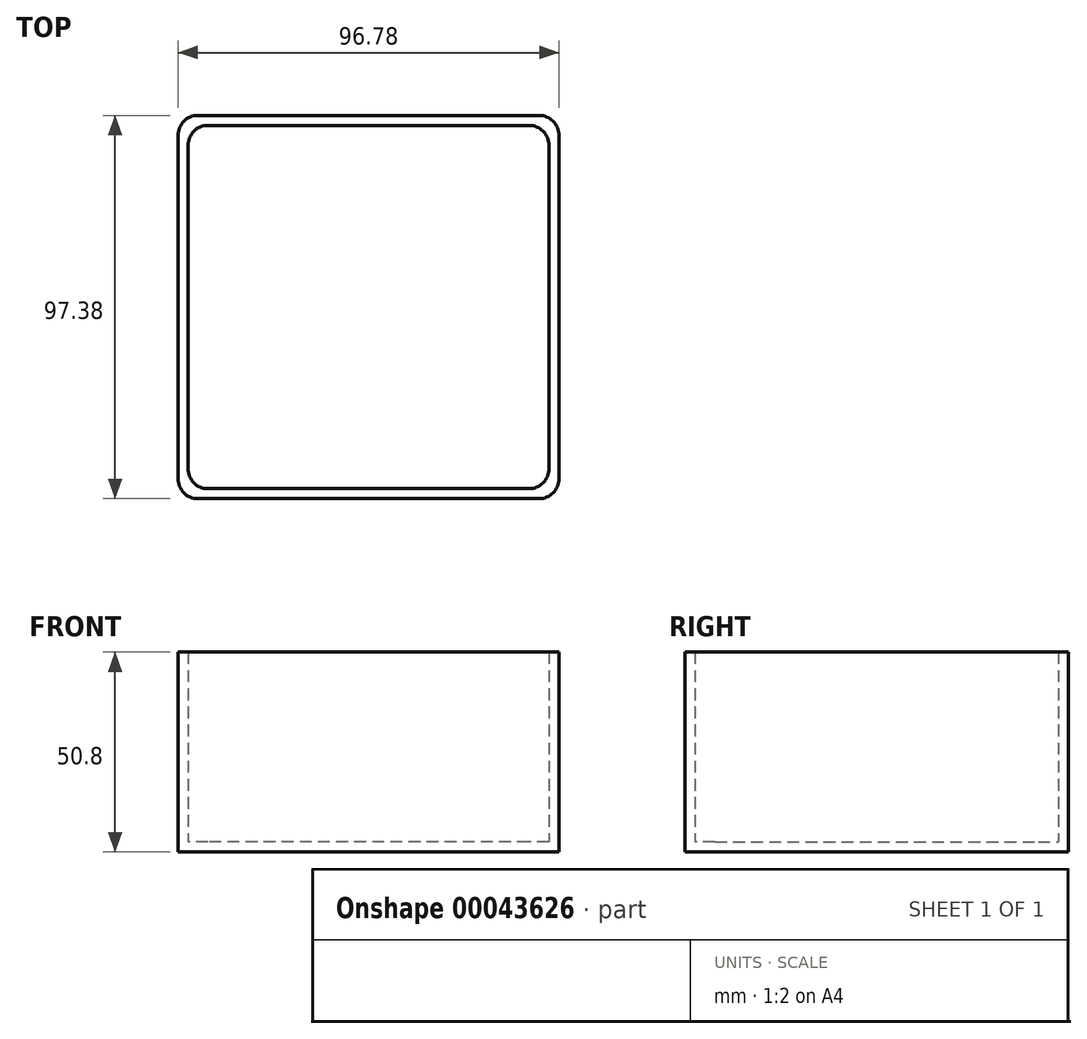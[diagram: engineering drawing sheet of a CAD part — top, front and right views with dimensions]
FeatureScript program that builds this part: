
annotation { "Feature Type Name" : "Feature", "Feature Type Description" : "" }
export const myFeature = defineFeature(function(context is Context, id is Id, definition is map)
    precondition{}
    {
        {
            var Q0;
            Q0=qCreatedBy(makeId("Top.planeOp"),FACE);
            var sketch = newSketch(context, id + "F0", { "sketchPlane" : qUnion([Q0])});
            skLineSegment(sketch, "E0.rect.bottom", {"start": v(48.4, -48.69) * mm, "end": v(-48.4, -48.69) * mm});
            skLineSegment(sketch, "E0.rect.top", {"start": v(48.4, 48.69) * mm, "end": v(-48.4, 48.69) * mm});
            skLineSegment(sketch, "E0.rect.left", {"start": v(48.4, -48.69) * mm, "end": v(48.4, 48.69) * mm});
            skLineSegment(sketch, "E0.rect.right", {"start": v(-48.4, -48.69) * mm, "end": v(-48.4, 48.69) * mm});
            skPoint(sketch, "E0.rect.middle", {"position": v(0, 0) * mm});
            skSolve(sketch);
        }
        {
            var Q0;
            Q0 = qSketchRegion(id + "F0", true);
            extrude(context, id + "F1", {"entities" : qUnion([Q0]), "depth" : 50.8 * mm});
        }
        {
            var Q0;
            Q0=makeQuery(id+"F1.opExtrude","CAP_FACE",FACE,{"disambiguationData":[OSD([sQuery(id+"F0.wireOp",EDGE,"E0.rect.bottom"),sQuery(id+"F0.wireOp",EDGE,"E0.rect.top"),sQuery(id+"F0.wireOp",EDGE,"E0.rect.left"),sQuery(id+"F0.wireOp",EDGE,"E0.rect.right")])],"isStart":false});
            shell(context, id + "F2", {"entities" : qUnion([Q0]), "thickness" : 2.54 * mm});
        }
        {
            var Q0;
            Q0=makeQuery(id+"F1.opExtrude","SWEPT_EDGE",EDGE,{"disambiguationData":[OSD([sQuery(id+"F0.wireOp",EDGE,"E0.rect.bottom"),sQuery(id+"F0.wireOp",EDGE,"E0.rect.right")])]});
            var Q1;
            Q1=makeQuery(id+"F1.opExtrude","SWEPT_EDGE",EDGE,{"disambiguationData":[OSD([sQuery(id+"F0.wireOp",EDGE,"E0.rect.top"),sQuery(id+"F0.wireOp",EDGE,"E0.rect.right")])]});
            var Q2;
            Q2=makeQuery(id+"F1.opExtrude","SWEPT_EDGE",EDGE,{"disambiguationData":[OSD([sQuery(id+"F0.wireOp",EDGE,"E0.rect.top"),sQuery(id+"F0.wireOp",EDGE,"E0.rect.left")])]});
            var Q3;
            Q3=makeQuery(id+"F1.opExtrude","SWEPT_EDGE",EDGE,{"disambiguationData":[OSD([sQuery(id+"F0.wireOp",EDGE,"E0.rect.bottom"),sQuery(id+"F0.wireOp",EDGE,"E0.rect.left")])]});
            fillet(context, id + "F3", {"entities" : qUnion([Q0, Q1, Q2, Q3]), "radius" : 5.08 * mm, "tangentPropagation" : true, "allowEdgeOverflow" : false});
        }
        {
            var Q0;
            Q0=makeQuery(id+"F2.opShell","OFFSET_EDGE",EDGE,{"disambiguationData":[OSD([sQuery(id+"F0.wireOp",EDGE,"E0.rect.bottom"),sQuery(id+"F0.wireOp",EDGE,"E0.rect.right")])]});
            var Q1;
            Q1=makeQuery(id+"F2.opShell","OFFSET_EDGE",EDGE,{"disambiguationData":[OSD([sQuery(id+"F0.wireOp",EDGE,"E0.rect.top"),sQuery(id+"F0.wireOp",EDGE,"E0.rect.right")])]});
            var Q2;
            Q2=makeQuery(id+"F2.opShell","OFFSET_EDGE",EDGE,{"disambiguationData":[OSD([sQuery(id+"F0.wireOp",EDGE,"E0.rect.bottom"),sQuery(id+"F0.wireOp",EDGE,"E0.rect.left")])]});
            var Q3;
            Q3=makeQuery(id+"F2.opShell","OFFSET_EDGE",EDGE,{"disambiguationData":[OSD([sQuery(id+"F0.wireOp",EDGE,"E0.rect.top"),sQuery(id+"F0.wireOp",EDGE,"E0.rect.left")])]});
            fillet(context, id + "F4", {"entities" : qUnion([Q0, Q1, Q2, Q3]), "radius" : 5.08 * mm, "tangentPropagation" : true, "allowEdgeOverflow" : false});
        }
    });
